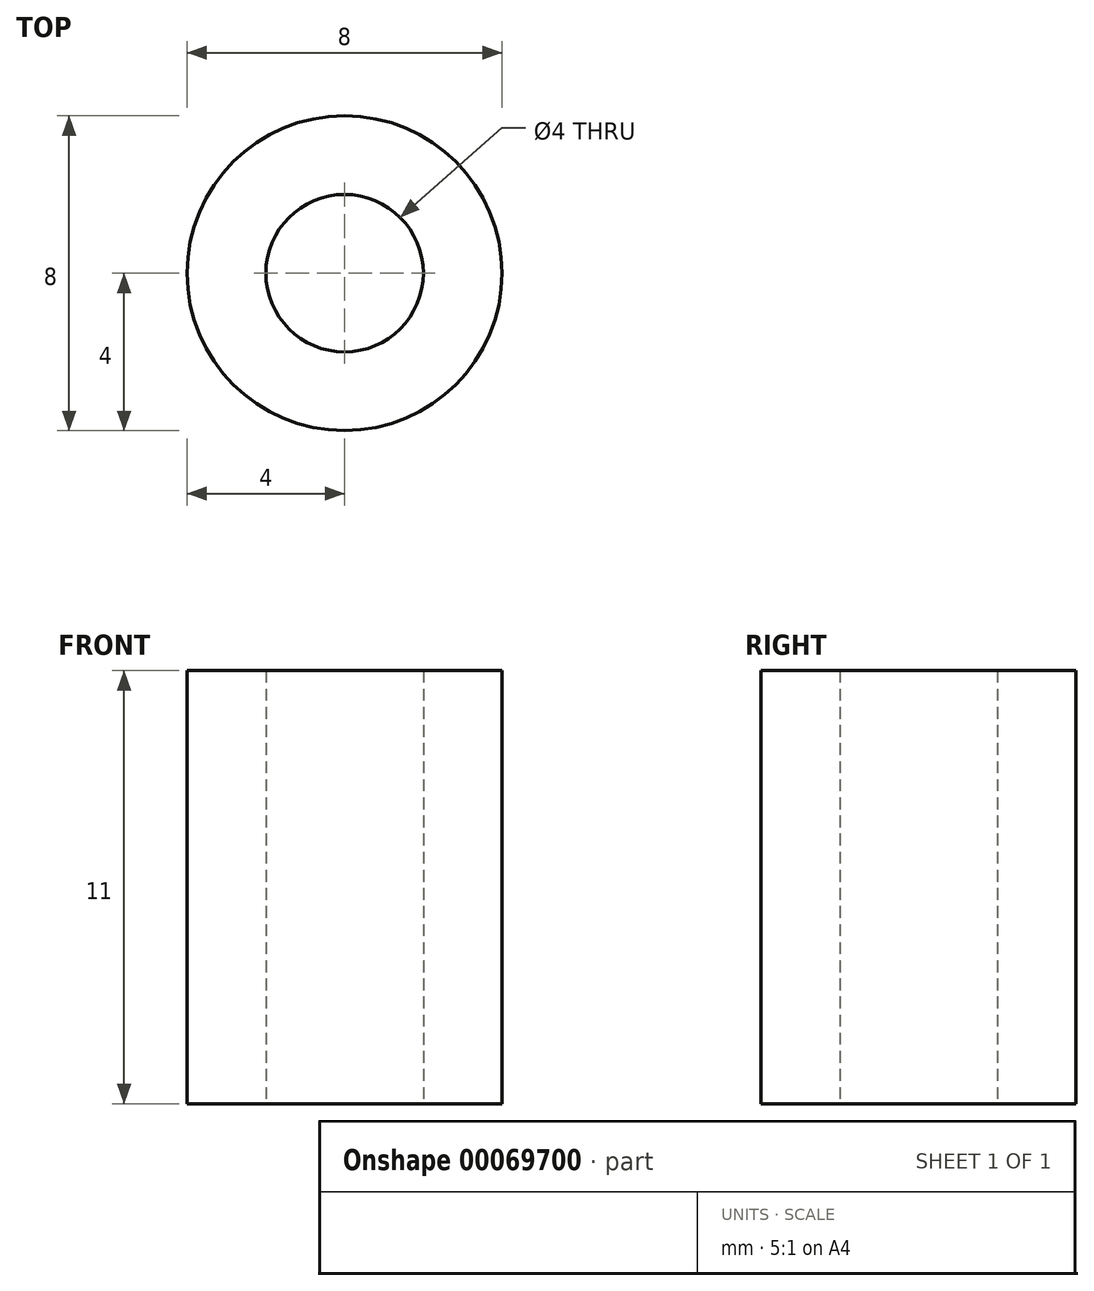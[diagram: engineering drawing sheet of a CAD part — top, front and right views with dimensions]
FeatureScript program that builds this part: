
annotation { "Feature Type Name" : "Feature", "Feature Type Description" : "" }
export const myFeature = defineFeature(function(context is Context, id is Id, definition is map)
    precondition{}
    {
        {
            var Q0;
            Q0=qCreatedBy(makeId("Top.planeOp"), FACE);
            var sketch = newSketch(context, id + "F0", { "sketchPlane" : qUnion([Q0])});
            skCircle(sketch, "E0", {"center": v(0, 0) * mm, "radius": 4 * mm});
            skCircle(sketch, "E1", {"center": v(0, 0) * mm, "radius": 2 * mm});
            skSolve(sketch);
        }
        {
            var Q0;
            Q0 = qSketchRegion(id + "F0", true);
            extrude(context, id + "F1", {"entities" : qUnion([Q0]), "depth" : 11 * mm, "offsetDistance" : 25 * mm});
        }
    });
